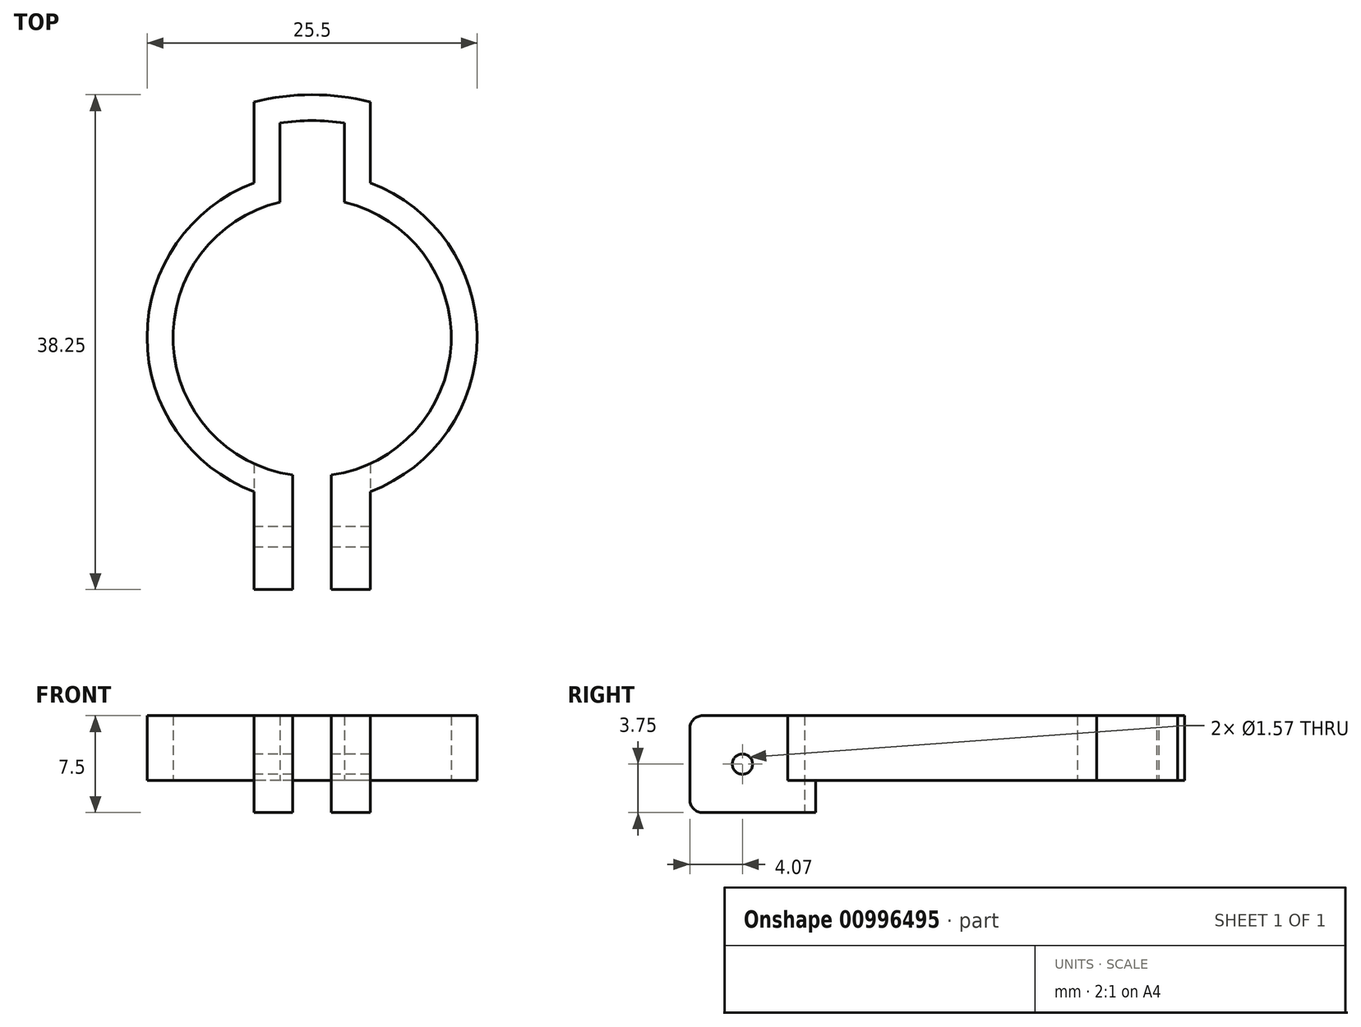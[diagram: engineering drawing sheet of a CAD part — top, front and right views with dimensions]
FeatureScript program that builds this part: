
annotation { "Feature Type Name" : "Feature", "Feature Type Description" : "" }
export const myFeature = defineFeature(function(context is Context, id is Id, definition is map)
    precondition{}
    {
        {
            var Q0;
            Q0=qCreatedBy(makeId("Top.planeOp"),FACE);
            var sketch = newSketch(context, id + "F0", { "sketchPlane" : qUnion([Q0])});
            skArc(sketch, "E0", {"start": v(-2.5, 10.46) * mm, "mid": v(0, -10.75) * mm, "end": v(2.5, 10.46) * mm});
            skArc(sketch, "E1", {"start": v(-4.5, 11.93) * mm, "mid": v(0, -12.75) * mm, "end": v(4.5, 11.93) * mm});
            skArc(sketch, "E2", {"start": v(4.5, 18.2) * mm, "mid": v(0, 18.75) * mm, "end": v(-4.5, 18.2) * mm});
            skLineSegment(sketch, "E3", {"start": v(-4.5, 18.2) * mm, "end": v(-4.5, 11.93) * mm});
            skLineSegment(sketch, "E4", {"start": v(0, 25.27) * mm, "end": v(0, -24.58) * mm, "construction": true});
            skLineSegment(sketch, "E5.MirrorCS", {"start": v(4.5, 18.2) * mm, "end": v(4.5, 11.93) * mm});
            skLineSegment(sketch, "E6", {"start": v(-2.5, 16.56) * mm, "end": v(-2.5, 10.46) * mm});
            skLineSegment(sketch, "E7.MirrorCS", {"start": v(2.5, 16.56) * mm, "end": v(2.5, 10.46) * mm});
            skPoint(sketch, "E8.orphan", {"position": v(-4.5, 23.62) * mm});
            skPoint(sketch, "E9.orphan", {"position": v(-2.5, 22.43) * mm});
            skPoint(sketch, "E10.orphan", {"position": v(2.5, 22.43) * mm});
            skPoint(sketch, "E11.orphan", {"position": v(4.5, 23.62) * mm});
            skPoint(sketch, "E12.orphan", {"position": v(-4.5, -28.06) * mm});
            skPoint(sketch, "E13.orphan", {"position": v(-2.5, -25.31) * mm});
            skPoint(sketch, "E14.orphan", {"position": v(2.5, -25.31) * mm});
            skPoint(sketch, "E15.orphan", {"position": v(4.5, -28.06) * mm});
            skArc(sketch, "E16.trimOffspring", {"start": v(2.5, 16.56) * mm, "mid": v(0, 16.75) * mm, "end": v(-2.5, 16.56) * mm});
            skSolve(sketch);
        }
        {
            var Q0;
            Q0=makeQuery(id+"F0.imprint","IMPRINT",FACE,{"disambiguationData":[TD([[makeQuery(id+"F0.imprint","IMPRINT",EDGE,{"derivedFrom":sQuery(id+"F0.wireOp",EDGE,"E0")}),-1.0]])]});
            extrude(context, id + "F1", {"entities" : qUnion([Q0]), "depth" : 5 * mm, "offsetDistance" : 25 * mm});
        }
        {
            var Q0;
            Q0=makeQuery(id+"F1.opExtrude","CAP_FACE",FACE,{"disambiguationData":[OSD([sQuery(id+"F0.wireOp",EDGE,"E0"),sQuery(id+"F0.wireOp",EDGE,"E1"),sQuery(id+"F0.wireOp",EDGE,"E2"),sQuery(id+"F0.wireOp",EDGE,"E3"),sQuery(id+"F0.wireOp",EDGE,"E5.MirrorCS"),sQuery(id+"F0.wireOp",EDGE,"E6"),sQuery(id+"F0.wireOp",EDGE,"E7.MirrorCS"),sQuery(id+"F0.wireOp",EDGE,"E16.trimOffspring")])],"isStart":false});
            var sketch = newSketch(context, id + "F2", { "sketchPlane" : qUnion([Q0])});
            skLineSegment(sketch, "E17.bottom", {"start": v(-4.5, -7.5) * mm, "end": v(4.5, -7.5) * mm});
            skLineSegment(sketch, "E17.top", {"start": v(-4.5, -19.5) * mm, "end": v(4.5, -19.5) * mm});
            skLineSegment(sketch, "E17.left", {"start": v(-4.5, -7.5) * mm, "end": v(-4.5, -19.5) * mm});
            skLineSegment(sketch, "E17.right", {"start": v(4.5, -7.5) * mm, "end": v(4.5, -19.5) * mm});
            skSolve(sketch);
        }
        {
            var Q0;
            {var subQ0=sQuery(id+"F2.wireOp",EDGE,"E17.left");var subQ1=makeQuery(id+"F1.opExtrude","CAP_EDGE",EDGE,{"disambiguationData":[OSD([sQuery(id+"F0.wireOp",EDGE,"E1")])],"isStart":false});var subQ2=makeQuery(id+"F2.imprint","INTERSECT",VERTEX,{"derivedFrom":[subQ1,subQ0]});Q0=makeQuery(id+"F2.imprint","IMPRINT",FACE,{"disambiguationData":[TD([[makeQuery(id+"F2.imprint","IMPRINT",EDGE,{"disambiguationData":[TD([[subQ2,1.0]])],"derivedFrom":subQ0}),1.0]])]});}
            var Q1;
            {var subQ0=sQuery(id+"F2.wireOp",EDGE,"E17.top");Q1=makeQuery(id+"F2.imprint","IMPRINT",FACE,{"disambiguationData":[TD([[makeQuery(id+"F2.imprint","IMPRINT",EDGE,{"derivedFrom":subQ0}),1.0]])]});}
            extrude(context, id + "F3", {"entities" : qUnion([Q0, Q1]), "operationType" : NewBodyOperationType.ADD, "oppositeDirection" : true, "depth" : 7.5 * mm, "offsetDistance" : 25 * mm});
        }
        {
            var Q0;
            Q0=makeQuery(id+"F1.opExtrude","CAP_FACE",FACE,{"disambiguationData":[OSD([sQuery(id+"F0.wireOp",EDGE,"E0"),sQuery(id+"F0.wireOp",EDGE,"E1"),sQuery(id+"F0.wireOp",EDGE,"E2"),sQuery(id+"F0.wireOp",EDGE,"E3"),sQuery(id+"F0.wireOp",EDGE,"E5.MirrorCS"),sQuery(id+"F0.wireOp",EDGE,"E6"),sQuery(id+"F0.wireOp",EDGE,"E7.MirrorCS"),sQuery(id+"F0.wireOp",EDGE,"E16.trimOffspring")])],"isStart":false});
            var sketch = newSketch(context, id + "F4", { "sketchPlane" : qUnion([Q0])});
            skLineSegment(sketch, "E18.bottom", {"start": v(-1.5, -8) * mm, "end": v(1.5, -8) * mm});
            skLineSegment(sketch, "E18.top", {"start": v(-1.5, -23) * mm, "end": v(1.5, -23) * mm});
            skLineSegment(sketch, "E18.left", {"start": v(-1.5, -8) * mm, "end": v(-1.5, -23) * mm});
            skLineSegment(sketch, "E18.right", {"start": v(1.5, -8) * mm, "end": v(1.5, -23) * mm});
            skSolve(sketch);
        }
        {
            var Q0;
            {var subQ0=sQuery(id+"F4.wireOp",EDGE,"E18.left");var subQ1=makeQuery(id+"F1.opExtrude","CAP_EDGE",EDGE,{"disambiguationData":[OSD([sQuery(id+"F0.wireOp",EDGE,"E1")])],"isStart":false});var subQ2=makeQuery(id+"F4.imprint","INTERSECT",VERTEX,{"derivedFrom":[subQ1,subQ0]});Q0=makeQuery(id+"F4.imprint","IMPRINT",FACE,{"disambiguationData":[TD([[makeQuery(id+"F4.imprint","IMPRINT",EDGE,{"disambiguationData":[TD([[subQ2,1.0]])],"derivedFrom":subQ0}),1.0]])]});}
            extrude(context, id + "F5", {"entities" : qUnion([Q0]), "operationType" : NewBodyOperationType.REMOVE, "endBound" : BoundingType.UP_TO_NEXT, "oppositeDirection" : true, "depth" : 25 * mm, "offsetDistance" : 25 * mm});
        }
        {
            var Q0;
            {var subQ0=sQuery(id+"F2.wireOp",EDGE,"E17.left");var subQ1=sQuery(id+"F2.wireOp",EDGE,"E17.top");Q0=makeQuery(id+"F5.boolean.opBoolean","SPLIT",EDGE,{"disambiguationData":[TD([makeQuery(id+"F3.opExtrude","SWEPT_FACE",FACE,{"disambiguationData":[OSD([subQ0])]})])],"derivedFrom":makeQuery(id+"F3.opExtrude","CAP_EDGE",EDGE,{"disambiguationData":[OSD([subQ1])],"isStart":true})});}
            var Q1;
            {var subQ0=sQuery(id+"F2.wireOp",EDGE,"E17.right");var subQ1=sQuery(id+"F2.wireOp",EDGE,"E17.top");Q1=makeQuery(id+"F5.boolean.opBoolean","SPLIT",EDGE,{"disambiguationData":[TD([makeQuery(id+"F3.opExtrude","SWEPT_FACE",FACE,{"disambiguationData":[OSD([subQ0])]})])],"derivedFrom":makeQuery(id+"F3.opExtrude","CAP_EDGE",EDGE,{"disambiguationData":[OSD([subQ1])],"isStart":true})});}
            var Q2;
            {var subQ0=sQuery(id+"F2.wireOp",EDGE,"E17.top");var subQ1=sQuery(id+"F2.wireOp",EDGE,"E17.right");Q2=makeQuery(id+"F5.boolean.opBoolean","SPLIT",EDGE,{"disambiguationData":[TD([makeQuery(id+"F3.opExtrude","SWEPT_FACE",FACE,{"disambiguationData":[OSD([subQ1])]})])],"derivedFrom":makeQuery(id+"F3.opExtrude","CAP_EDGE",EDGE,{"disambiguationData":[OSD([subQ0])],"isStart":false})});}
            var Q3;
            {var subQ0=sQuery(id+"F2.wireOp",EDGE,"E17.top");var subQ1=sQuery(id+"F2.wireOp",EDGE,"E17.left");Q3=makeQuery(id+"F5.boolean.opBoolean","SPLIT",EDGE,{"disambiguationData":[TD([makeQuery(id+"F3.opExtrude","SWEPT_FACE",FACE,{"disambiguationData":[OSD([subQ1])]})])],"derivedFrom":makeQuery(id+"F3.opExtrude","CAP_EDGE",EDGE,{"disambiguationData":[OSD([subQ0])],"isStart":false})});}
            fillet(context, id + "F6", {"entities" : qUnion([Q0, Q1, Q2, Q3]), "radius" : 1 * mm, "tangentPropagation" : true, "allowEdgeOverflow" : false});
        }
        {
            var Q0;
            Q0=makeQuery(id+"F3.opExtrude","SWEPT_FACE",FACE,{"disambiguationData":[OSD([sQuery(id+"F2.wireOp",EDGE,"E17.left")])]});
            var sketch = newSketch(context, id + "F7", { "sketchPlane" : qUnion([Q0])});
            skCircle(sketch, "E19", {"center": v(15.43, 1.25) * mm, "radius": 0.78 * mm});
            skSolve(sketch);
        }
        {
            var Q0;
            Q0=makeQuery(id+"F7.imprint","IMPRINT",FACE,{"disambiguationData":[TD([[makeQuery(id+"F7.imprint","IMPRINT",EDGE,{"derivedFrom":sQuery(id+"F7.wireOp",EDGE,"E19")}),1.0]])]});
            extrude(context, id + "F8", {"entities" : qUnion([Q0]), "operationType" : NewBodyOperationType.REMOVE, "oppositeDirection" : true, "depth" : 25 * mm, "offsetDistance" : 25 * mm});
        }
    });
